# Revit family: Screens-Leg_Mounted-Teknion-JNSFGL_Floor_Screen-R20161
name_source: partatom
category: Furniture
revit_build: Autodesk Revit Architecture 2016 (Build: 20150714_1515(x64)
units: mm (PartAtom-declared; Revit-internal decimal feet)

## family parameters
Always vertical = Yes
Cut with Voids When Loaded = No
OmniClass Number = 23.40.70.14.64.21
OmniClass Title = Systems Furniture
Room Calculation Point = No
Shared = Yes
Work Plane-Based = No

## types (3) — shared parameters
Assembly Code = E2020200
Manufacturer = Teknion
Manufacturer Fax = 416.661.4586
Product Documentation Link = https://www.teknion.com
Product Line = Expansion Cityline
Product Page URL = https://www.teknion.com
Series = Expansion Cityline
Sustainability Data = https://www.teknion.com
URL = www.teknion.com
Unit Weight URL = http://www.teknion.com
Warranty = http://www.teknion.com

## per-type parameters (varying)
| type | Description | Left | Left Bracket Visiblity | Model | Right | Right Bracket Visiblity |
| Double-Sided Leg Overlay | Floor Screen with Glass – Leg-Mounted, Double-Sided Leg Overlay | No | Yes | JNSFGLD_____ | No | Yes |
| Left Configuration | Floor Screen with Glass – Leg-Mounted, Left Configuration | Yes | No | JNSFGLL_____ | No | Yes |
| Right Configuration | Floor Screen with Glass – Leg-Mounted, Right Configuration | No | Yes | JNSFGLR_____ | Yes | No |

type visibility flags (boolean, named after types; folded from table):
- Double-Sided Leg Overlay: Yes: Double-Sided Leg Overlay
- Left Configuration: Yes: (none)
- Right Configuration: Yes: (none)

## geometry (parser evidence)
native form markers: Sweep x2
no freeform markers — native parametric forms only
